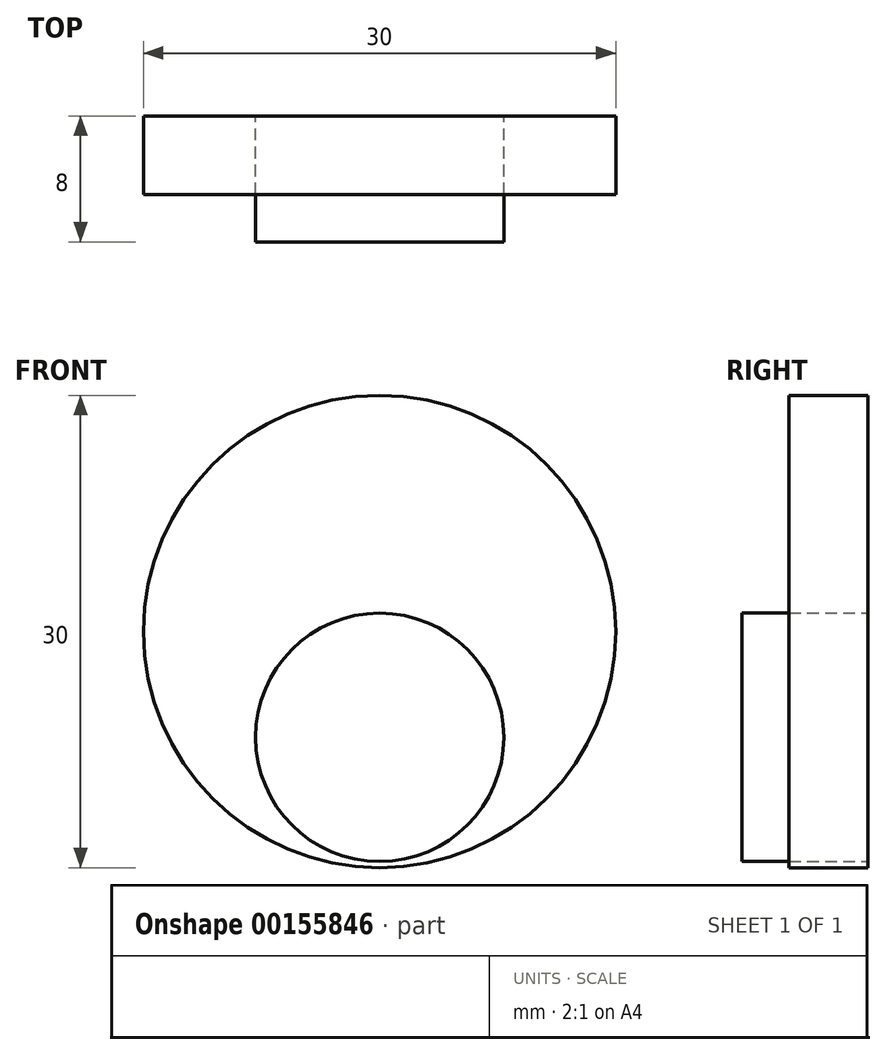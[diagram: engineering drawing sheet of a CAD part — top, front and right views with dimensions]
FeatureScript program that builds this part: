
annotation { "Feature Type Name" : "Feature", "Feature Type Description" : "" }
export const myFeature = defineFeature(function(context is Context, id is Id, definition is map)
    precondition{}
    {
        {
            var Q0;
            Q0=qCreatedBy(makeId("Front.planeOp"),FACE);
            var sketch = newSketch(context, id + "F0", { "sketchPlane" : qUnion([Q0])});
            skCircle(sketch, "E0", {"center": v(-47.35, 0) * mm, "radius": 15 * mm});
            skCircle(sketch, "E1", {"center": v(-47.35, -6.72) * mm, "radius": 7.88 * mm});
            skSolve(sketch);
        }
        {
            var Q0;
            Q0=makeQuery(id+"F0.imprint","IMPRINT",FACE,{"disambiguationData":[TD([[makeQuery(id+"F0.imprint","IMPRINT",EDGE,{"derivedFrom":sQuery(id+"F0.wireOp",EDGE,"E0")}),1.0]])]});
            var Q1;
            Q1=makeQuery(id+"F0.imprint","IMPRINT",FACE,{"disambiguationData":[TD([[makeQuery(id+"F0.imprint","IMPRINT",EDGE,{"derivedFrom":sQuery(id+"F0.wireOp",EDGE,"E1")}),1.0]])]});
            extrude(context, id + "F1", {"entities" : qUnion([Q0, Q1]), "depth" : 5 * mm});
        }
        {
            var Q0;
            Q0=makeQuery(id+"F0.imprint","IMPRINT",FACE,{"disambiguationData":[TD([[makeQuery(id+"F0.imprint","IMPRINT",EDGE,{"derivedFrom":sQuery(id+"F0.wireOp",EDGE,"E1")}),1.0]])]});
            extrude(context, id + "F2", {"entities" : qUnion([Q0]), "depth" : 8 * mm});
        }
    });
